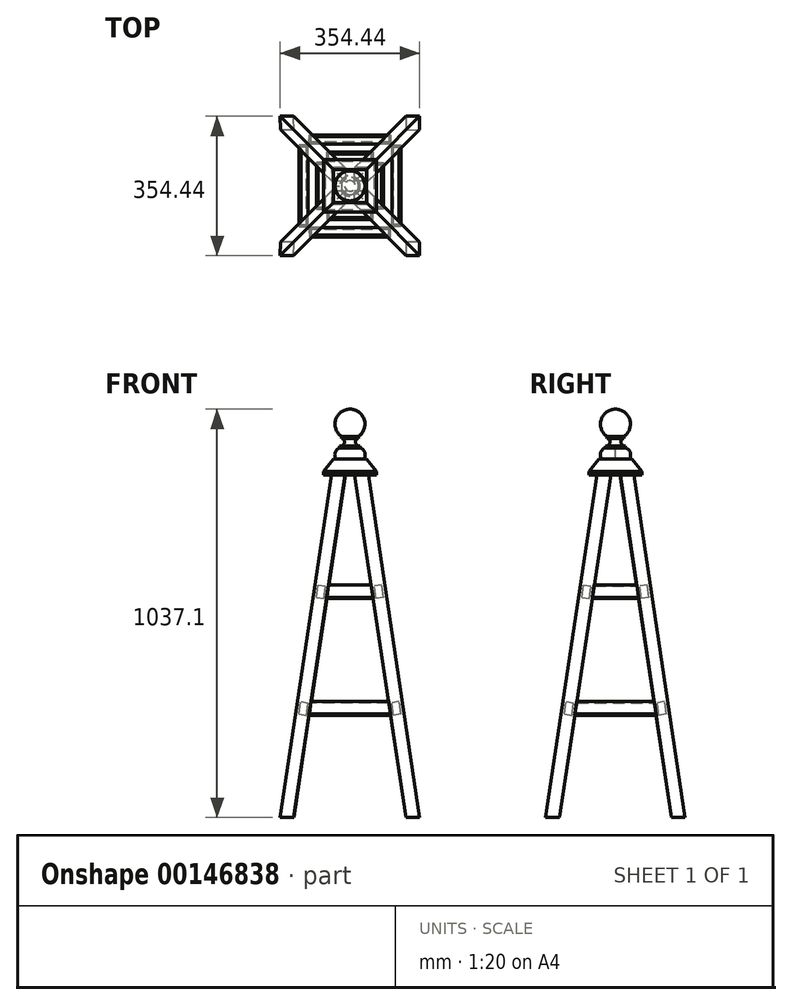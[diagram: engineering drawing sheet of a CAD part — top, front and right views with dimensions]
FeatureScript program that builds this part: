
annotation { "Feature Type Name" : "Feature", "Feature Type Description" : "" }
export const myFeature = defineFeature(function(context is Context, id is Id, definition is map)
    precondition{}
    {
        {
            assignVariable(context, id + "F0", {"name" : "Angle0", "anyValue" : 12 * degree});
        }
        {
            assignVariable(context, id + "F1", {"name" : "CentreSpread0", "anyValue" : 12});
        }
        {
            assignVariable(context, id + "F2", {"name" : "ArmOffset0", "anyValue" : ((((900 - (sqrt(34 * 34 * 2) * sin(getVariable(context, 'Angle0')))) * sin(getVariable(context, 'Angle0')) + (sqrt(17 * 17 * 2) / cos(getVariable(context, 'Angle0')))) * sin(45 * degree)) + getVariable(context, 'CentreSpread0')) * mm});
        }
        {
            var Q0;
            Q0=qCreatedBy(makeId("Front.planeOp"),FACE);
            var sketch = newSketch(context, id + "F3", { "sketchPlane" : qUnion([Q0])});
            skLineSegment(sketch, "E0.bottom", {"start": v(-17, 450) * mm, "end": v(17, 450) * mm});
            skLineSegment(sketch, "E0.top", {"start": v(-17, -450) * mm, "end": v(17, -450) * mm});
            skLineSegment(sketch, "E0.left", {"start": v(-17, 450) * mm, "end": v(-17, -450) * mm});
            skLineSegment(sketch, "E0.right", {"start": v(17, 450) * mm, "end": v(17, -450) * mm});
            skPoint(sketch, "E0.middle", {"position": v(0, 0) * mm});
            skLineSegment(sketch, "E1", {"start": v(0, 0) * mm, "end": v(0, 406.37) * mm, "construction": true});
            skSolve(sketch);
        }
        {
            var Q0;
            Q0=sQuery(id+"F3.wireOp",EDGE,"E1");
            cPlane(context, id + "F4", {"entities" : qUnion([Q0]), "cplaneType" : CPlaneType.LINE_ANGLE, "offset" : 25 * mm, "angle" : 45 * degree, "width" : 150 * mm, "height" : 150 * mm});
        }
        {
            var Q0;
            Q0=sQuery(id+"F3.wireOp",EDGE,"E1");
            cPlane(context, id + "F5", {"entities" : qUnion([Q0]), "cplaneType" : CPlaneType.LINE_ANGLE, "offset" : 25 * mm, "angle" : 135 * degree, "width" : 150 * mm, "height" : 150 * mm});
        }
        {
            var Q0;
            Q0=qCreatedBy(id+"F5.planeOp",FACE);
            cPlane(context, id + "F6", {"entities" : qUnion([Q0]), "cplaneType" : CPlaneType.OFFSET, "offset" : (sqrt(17 * 17 * 2)) * mm, "oppositeDirection" : true, "width" : 150 * mm, "height" : 150 * mm});
        }
        {
            var Q0;
            Q0=qSketchRegion(id+"F3",true);
            extrude(context, id + "F7", {"entities" : qUnion([Q0]), "depth" : 17 * mm, "hasSecondDirection" : true, "secondDirectionOppositeDirection" : true, "secondDirectionDepth" : 17 * mm});
        }
        {
            var Q0;
            Q0=qCreatedBy(id+"F4.planeOp",FACE);
            var sketch = newSketch(context, id + "F8", { "sketchPlane" : qUnion([Q0])});
            skLineSegment(sketch, "E2", {"start": v(24.04, 450) * mm, "end": v(-24.04, 439.78) * mm});
            skLineSegment(sketch, "E3", {"start": v(-24.04, 450) * mm, "end": v(24.04, 450) * mm});
            skLineSegment(sketch, "E4", {"start": v(-24.04, 450) * mm, "end": v(-24.04, 439.78) * mm});
            skLineSegment(sketch, "E5", {"start": v(-24.04, -450) * mm, "end": v(24.04, -439.78) * mm});
            skLineSegment(sketch, "E6", {"start": v(-24.04, -450) * mm, "end": v(24.04, -450) * mm});
            skLineSegment(sketch, "E7", {"start": v(24.04, -450) * mm, "end": v(24.04, -439.78) * mm});
            skSolve(sketch);
        }
        {
            var Q0;
            Q0=qSketchRegion(id+"F8",true);
            extrude(context, id + "F9", {"entities" : qUnion([Q0]), "operationType" : NewBodyOperationType.REMOVE, "depth" : (sqrt(17 * 17 * 2)) * mm, "hasSecondDirection" : true, "secondDirectionOppositeDirection" : true, "secondDirectionDepth" : (sqrt(17 * 17 * 2)) * mm});
        }
        {
            var Q0;
            Q0=qCreatedBy(id+"F6.planeOp",FACE);
            var sketch = newSketch(context, id + "F10", { "sketchPlane" : qUnion([Q0])});
            skLineSegment(sketch, "E8", {"start": v(-24.04, -450) * mm, "end": v(24.04, -450) * mm, "construction": true});
            skSolve(sketch);
        }
        {
            var Q0;
            Q0=makeQuery(id+"F7.opExtrude","SWEPT_BODY",BODY,{"disambiguationData":[OSD([sQuery(id+"F3.wireOp",EDGE,"E0.bottom"),sQuery(id+"F3.wireOp",EDGE,"E0.top"),sQuery(id+"F3.wireOp",EDGE,"E0.left"),sQuery(id+"F3.wireOp",EDGE,"E0.right")])]});
            var Q1;
            Q1=sQuery(id+"F10.wireOp",EDGE,"E8");
            transform(context, id + "F11", {"entities" : qUnion([Q0]), "transformType" : TransformType.ROTATION, "transformAxis" : qUnion([Q1]), "angle" : getVariable(context, 'Angle0'), "makeCopy" : false});
        }
        {
            var Q0;
            Q0=makeQuery(id+"F7.opExtrude","SWEPT_BODY",BODY,{"disambiguationData":[OSD([sQuery(id+"F3.wireOp",EDGE,"E0.bottom"),sQuery(id+"F3.wireOp",EDGE,"E0.top"),sQuery(id+"F3.wireOp",EDGE,"E0.left"),sQuery(id+"F3.wireOp",EDGE,"E0.right")])]});
            transform(context, id + "F12", {"entities" : qUnion([Q0]), "transformType" : TransformType.TRANSLATION_3D, "dx" : getVariable(context, 'ArmOffset0'), "dy" : -getVariable(context, 'ArmOffset0'), "dz" : 0 * mm, "makeCopy" : false});
        }
        {
            var Q0;
            Q0=makeQuery(id+"F7.opExtrude","SWEPT_BODY",BODY,{"disambiguationData":[OSD([sQuery(id+"F3.wireOp",EDGE,"E0.bottom"),sQuery(id+"F3.wireOp",EDGE,"E0.top"),sQuery(id+"F3.wireOp",EDGE,"E0.left"),sQuery(id+"F3.wireOp",EDGE,"E0.right")])]});
            var Q1;
            Q1=sQuery(id+"F3.wireOp",EDGE,"E1");
            circularPattern(context, id + "F13", {"entities" : qUnion([Q0]), "axis" : qUnion([Q1]), "angle" : 360 * degree, "instanceCount" : 4, "equalSpace" : true});
        }
        {
            var Q0;
            Q0=qCreatedBy(makeId("Top.planeOp"),FACE);
            var sketch = newSketch(context, id + "F14", { "sketchPlane" : qUnion([Q0])});
            skLineSegment(sketch, "E9.bottom", {"start": v(67, 67) * mm, "end": v(-67, 67) * mm});
            skLineSegment(sketch, "E9.top", {"start": v(67, -67) * mm, "end": v(-67, -67) * mm});
            skLineSegment(sketch, "E9.left", {"start": v(67, 67) * mm, "end": v(67, -67) * mm});
            skLineSegment(sketch, "E9.right", {"start": v(-67, 67) * mm, "end": v(-67, -67) * mm});
            skPoint(sketch, "E9.middle", {"position": v(0, 0) * mm});
            skSolve(sketch);
        }
        {
            var Q0;
            Q0=qSketchRegion(id+"F14",true);
            extrude(context, id + "F15", {"entities" : qUnion([Q0]), "depth" : 32 * mm, "hasDraft" : true, "draftAngle" : 38 * degree, "draftPullDirection" : true, "hasSecondDirection" : true, "secondDirectionOppositeDirection" : true, "secondDirectionDepth" : 8 * mm});
        }
        {
            var Q0;
            Q0=makeQuery(id+"F15.split0.splitOp","SPLIT",BODY,{"derivedFrom":makeQuery(id+"F15.opExtrude","SWEPT_BODY",BODY,{"disambiguationData":[OSD([sQuery(id+"F14.wireOp",EDGE,"E9.bottom"),sQuery(id+"F14.wireOp",EDGE,"E9.top"),sQuery(id+"F14.wireOp",EDGE,"E9.left"),sQuery(id+"F14.wireOp",EDGE,"E9.right")])]})});
            transform(context, id + "F16", {"entities" : qUnion([Q0]), "transformType" : TransformType.TRANSLATION_3D, "dx" : 0 * mm, "dy" : 0 * mm, "dz" : ((900 * cos(getVariable(context, 'Angle0')) - (tan(getVariable(context, 'Angle0')) * sqrt(34 * 34 * 2)) - 442)) * mm, "makeCopy" : false});
        }
        {
            var Q0;
            Q0=qCreatedBy(makeId("Front.planeOp"),FACE);
            var sketch = newSketch(context, id + "F17", { "sketchPlane" : qUnion([Q0])});
            skLineSegment(sketch, "E10", {"start": v(0, 0) * mm, "end": v(33, 0) * mm});
            skFitSpline(sketch, "E11", {"points": [v(33, 0) * mm, v(38, 16.22) * mm, v(26, 28) * mm], "startDerivative": vector(25.56, 0) * mm, "endDerivative": vector(-18.97, 0) * mm});
            skLineSegment(sketch, "E12", {"start": v(26, 28) * mm, "end": v(26, 33) * mm});
            skFitSpline(sketch, "E13", {"points": [v(26, 33) * mm, v(13.8, 42.6) * mm, v(22, 53) * mm], "startDerivative": vector(-39.34, 1.43) * mm, "endDerivative": vector(35.56, 0.88) * mm});
            skLineSegment(sketch, "E14", {"start": v(22, 53) * mm, "end": v(22, 58) * mm});
            skArc(sketch, "E15", {"start": v(22, 58) * mm, "mid": v(36.2, 100.53) * mm, "end": v(0, 126.98) * mm});
            skLineSegment(sketch, "E16", {"start": v(0, 0) * mm, "end": v(0, 126.98) * mm});
            skSolve(sketch);
        }
        {
            var Q0;
            Q0=makeQuery(id+"F17.imprint","IMPRINT",FACE,{"disambiguationData":[TD([[makeQuery(id+"F17.imprint","IMPRINT",EDGE,{"derivedFrom":sQuery(id+"F17.wireOp",EDGE,"E10")}),1.0]])]});
            var Q1;
            Q1=sQuery(id+"F17.wireOp",EDGE,"E16");
            revolve(context, id + "F18", {"entities" : qUnion([Q0]), "axis" : qUnion([Q1]), "revolveType" : RevolveType.FULL});
        }
        {
            var Q0;
            Q0=makeQuery(id+"F18.opRevolve","SWEPT_BODY",BODY,{"disambiguationData":[OSD([sQuery(id+"F17.wireOp",EDGE,"E10"),sQuery(id+"F17.wireOp",EDGE,"E11"),sQuery(id+"F17.wireOp",EDGE,"E12"),sQuery(id+"F17.wireOp",EDGE,"E13"),sQuery(id+"F17.wireOp",EDGE,"E14"),sQuery(id+"F17.wireOp",EDGE,"E15"),sQuery(id+"F17.wireOp",EDGE,"E16")])]});
            transform(context, id + "F19", {"entities" : qUnion([Q0]), "transformType" : TransformType.TRANSLATION_3D, "dx" : 0 * mm, "dy" : 0 * mm, "dz" : ((900 * cos(getVariable(context, 'Angle0')) - (tan(getVariable(context, 'Angle0')) * sqrt(34 * 34 * 2)) - 410)) * mm, "makeCopy" : false});
        }
        {
            var Q0;
            Q0=qCreatedBy(makeId("Front.planeOp"),FACE);
            var sketch = newSketch(context, id + "F20", { "sketchPlane" : qUnion([Q0])});
            skLineSegment(sketch, "E17", {"start": v(0, -450) * mm, "end": v(0, 420.11) * mm, "construction": true});
            skLineSegment(sketch, "E18", {"start": v(-29.38, 420.11) * mm, "end": v(-29.38, -450) * mm, "construction": true});
            skLineSegment(sketch, "E19.bottom", {"start": v(-85.4, 108.97) * mm, "end": v(-66.61, 106.17) * mm});
            skLineSegment(sketch, "E19.top", {"start": v(-80.68, 140.62) * mm, "end": v(-61.89, 137.82) * mm});
            skLineSegment(sketch, "E19.left", {"start": v(-85.4, 108.97) * mm, "end": v(-80.68, 140.62) * mm});
            skLineSegment(sketch, "E19.right", {"start": v(-66.61, 106.17) * mm, "end": v(-61.89, 137.82) * mm});
            skPoint(sketch, "E19.middle", {"position": v(-73.65, 123.4) * mm});
            skLineSegment(sketch, "E20.MirrorCS", {"start": v(66.61, 106.17) * mm, "end": v(61.89, 137.82) * mm});
            skLineSegment(sketch, "E21.MirrorCS", {"start": v(85.4, 108.97) * mm, "end": v(66.61, 106.17) * mm});
            skLineSegment(sketch, "E22.MirrorCS", {"start": v(85.4, 108.97) * mm, "end": v(80.68, 140.62) * mm});
            skLineSegment(sketch, "E23.MirrorCS", {"start": v(80.68, 140.62) * mm, "end": v(61.89, 137.82) * mm});
            skLineSegment(sketch, "E24", {"start": v(-29.38, 420.11) * mm, "end": v(-159.2, -450) * mm, "construction": true});
            skLineSegment(sketch, "E25.bottom", {"start": v(-129.67, -187.74) * mm, "end": v(-110.88, -190.55) * mm});
            skLineSegment(sketch, "E25.top", {"start": v(-124.95, -156.1) * mm, "end": v(-106.16, -158.9) * mm});
            skLineSegment(sketch, "E25.left", {"start": v(-129.67, -187.74) * mm, "end": v(-124.95, -156.1) * mm});
            skLineSegment(sketch, "E25.right", {"start": v(-110.88, -190.55) * mm, "end": v(-106.16, -158.9) * mm});
            skPoint(sketch, "E25.middle", {"position": v(-117.91, -173.32) * mm});
            skLineSegment(sketch, "E26.MirrorCS", {"start": v(129.67, -187.74) * mm, "end": v(124.95, -156.1) * mm});
            skLineSegment(sketch, "E27.MirrorCS", {"start": v(129.67, -187.74) * mm, "end": v(110.88, -190.55) * mm});
            skLineSegment(sketch, "E28.MirrorCS", {"start": v(110.88, -190.55) * mm, "end": v(106.16, -158.9) * mm});
            skLineSegment(sketch, "E29.MirrorCS", {"start": v(124.95, -156.1) * mm, "end": v(106.16, -158.9) * mm});
            skSolve(sketch);
        }
        {
            var Q0;
            Q0=qSketchRegion(id+"F20",true);
            extrude(context, id + "F21", {"entities" : qUnion([Q0]), "endBound" : BoundingType.UP_TO_NEXT, "depth" : 25 * mm, "hasSecondDirection" : true, "secondDirectionBound" : SecondDirectionBoundingType.UP_TO_NEXT, "secondDirectionOppositeDirection" : true, "secondDirectionDepth" : 25 * mm});
        }
        {
            var Q0;
            Q0=makeQuery(id+"F21.opExtrude","SWEPT_BODY",BODY,{"disambiguationData":[OSD([sQuery(id+"F20.wireOp",EDGE,"E19.bottom"),sQuery(id+"F20.wireOp",EDGE,"E19.top"),sQuery(id+"F20.wireOp",EDGE,"E19.left"),sQuery(id+"F20.wireOp",EDGE,"E19.right")])]});
            var Q1;
            Q1=makeQuery(id+"F21.opExtrude","SWEPT_BODY",BODY,{"disambiguationData":[OSD([sQuery(id+"F20.wireOp",EDGE,"E20.MirrorCS"),sQuery(id+"F20.wireOp",EDGE,"E21.MirrorCS"),sQuery(id+"F20.wireOp",EDGE,"E22.MirrorCS"),sQuery(id+"F20.wireOp",EDGE,"E23.MirrorCS")])]});
            var Q2;
            Q2=makeQuery(id+"F21.opExtrude","SWEPT_BODY",BODY,{"disambiguationData":[OSD([sQuery(id+"F20.wireOp",EDGE,"HaTDqeZX-q0q9-RBWl-f2qk-jXWemIDRsZmG.bottom"),sQuery(id+"F20.wireOp",EDGE,"HaTDqeZX-q0q9-RBWl-f2qk-jXWemIDRsZmG.top"),sQuery(id+"F20.wireOp",EDGE,"HaTDqeZX-q0q9-RBWl-f2qk-jXWemIDRsZmG.left"),sQuery(id+"F20.wireOp",EDGE,"HaTDqeZX-q0q9-RBWl-f2qk-jXWemIDRsZmG.right")])]});
            var Q3;
            Q3=makeQuery(id+"F21.opExtrude","SWEPT_BODY",BODY,{"disambiguationData":[OSD([sQuery(id+"F20.wireOp",EDGE,"E25.bottom"),sQuery(id+"F20.wireOp",EDGE,"E25.top"),sQuery(id+"F20.wireOp",EDGE,"E25.left"),sQuery(id+"F20.wireOp",EDGE,"E25.right")])]});
            var Q4;
            Q4=makeQuery(id+"F21.opExtrude","SWEPT_BODY",BODY,{"disambiguationData":[OSD([sQuery(id+"F20.wireOp",EDGE,"E26.MirrorCS"),sQuery(id+"F20.wireOp",EDGE,"E27.MirrorCS"),sQuery(id+"F20.wireOp",EDGE,"E28.MirrorCS"),sQuery(id+"F20.wireOp",EDGE,"E29.MirrorCS")])]});
            var Q5;
            Q5=makeQuery(id+"F21.opExtrude","SWEPT_BODY",BODY,{"disambiguationData":[OSD([sQuery(id+"F20.wireOp",EDGE,"7501d314-7c19-41cf-ad6d-b390637c75b14.MirrorCS"),sQuery(id+"F20.wireOp",EDGE,"7501d314-7c19-41cf-ad6d-b390637c75b15.MirrorCS"),sQuery(id+"F20.wireOp",EDGE,"7501d314-7c19-41cf-ad6d-b390637c75b16.MirrorCS"),sQuery(id+"F20.wireOp",EDGE,"7501d314-7c19-41cf-ad6d-b390637c75b17.MirrorCS")])]});
            var Q6;
            Q6=sQuery(id+"F20.wireOp",EDGE,"E17");
            transform(context, id + "F22", {"entities" : qUnion([Q0, Q1, Q2, Q3, Q4, Q5]), "transformType" : TransformType.ROTATION, "transformAxis" : qUnion([Q6]), "angle" : 90 * degree, "makeCopy" : true});
        }
    });
